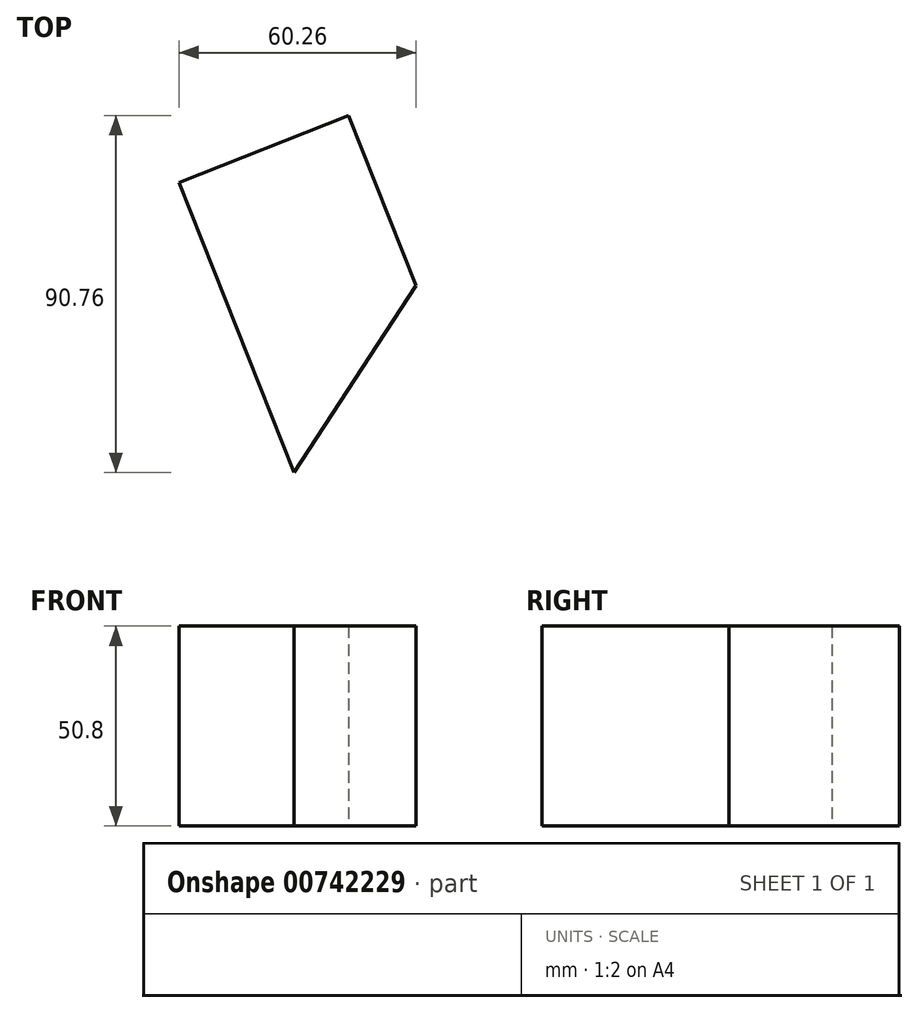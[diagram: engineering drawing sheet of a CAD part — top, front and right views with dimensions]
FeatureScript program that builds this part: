
annotation { "Feature Type Name" : "Feature", "Feature Type Description" : "" }
export const myFeature = defineFeature(function(context is Context, id is Id, definition is map)
    precondition{}
    {
        {
            var Q0;
            Q0=qCreatedBy(makeId("Top.planeOp"),FACE);
            var sketch = newSketch(context, id + "F0", { "sketchPlane" : qUnion([Q0])});
            skLineSegment(sketch, "E0", {"start": v(-17.5, 26.13) * mm, "end": v(25.64, 43.22) * mm});
            skLineSegment(sketch, "E1", {"start": v(25.64, 43.22) * mm, "end": v(42.76, 0) * mm});
            skLineSegment(sketch, "E2", {"start": v(42.76, 0) * mm, "end": v(11.8, -47.54) * mm});
            skLineSegment(sketch, "E3", {"start": v(11.8, -47.54) * mm, "end": v(-17.5, 26.13) * mm});
            skSolve(sketch);
        }
        {
            var Q0;
            Q0=makeQuery(id+"F0.imprint","IMPRINT",FACE,{"disambiguationData":[TD([[makeQuery(id+"F0.imprint","IMPRINT",EDGE,{"derivedFrom":sQuery(id+"F0.wireOp",EDGE,"E0")}),-1.0]])]});
            extrude(context, id + "F1", {"entities" : qUnion([Q0]), "depth" : 50.8 * mm, "offsetDistance" : 25.4 * mm});
        }
    });
